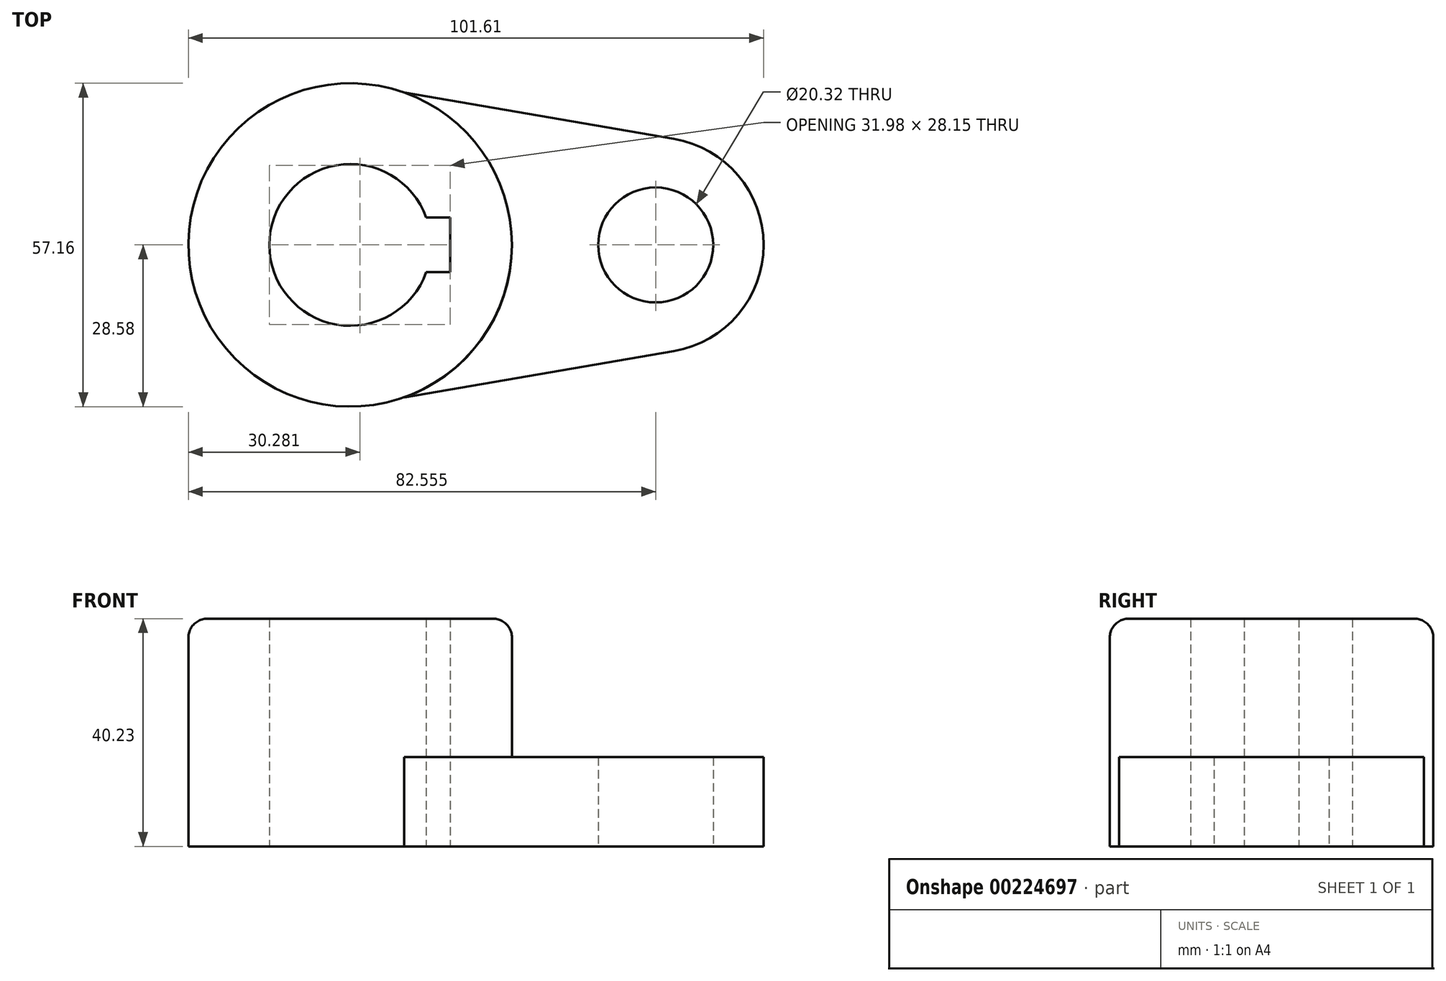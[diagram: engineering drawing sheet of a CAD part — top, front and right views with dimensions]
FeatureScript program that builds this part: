
annotation { "Feature Type Name" : "Feature", "Feature Type Description" : "" }
export const myFeature = defineFeature(function(context is Context, id is Id, definition is map)
    precondition{}
    {
        {
            var Q0;
            Q0=qCreatedBy(makeId("Top.planeOp"),FACE);
            var sketch = newSketch(context, id + "F0", { "sketchPlane" : qUnion([Q0])});
            skArc(sketch, "E0", {"start": v(13.45, 4.83) * mm, "mid": v(-14.29, 0) * mm, "end": v(13.45, -4.83) * mm});
            skCircle(sketch, "E1", {"center": v(53.98, 0) * mm, "radius": 10.16 * mm});
            skCircle(sketch, "E2", {"center": v(0, 0) * mm, "radius": 28.58 * mm});
            skLineSegment(sketch, "E3.bottom", {"start": v(17.69, 4.83) * mm, "end": v(13.45, 4.83) * mm});
            skLineSegment(sketch, "E3.top", {"start": v(17.69, -4.83) * mm, "end": v(13.45, -4.83) * mm});
            skLineSegment(sketch, "E3.left", {"start": v(17.69, 4.83) * mm, "end": v(17.69, -4.83) * mm});
            skPoint(sketch, "E3.right.end.orphan", {"position": v(-13.45, -4.83) * mm});
            skPoint(sketch, "E4.orphan", {"position": v(0, 28.58) * mm});
            skPoint(sketch, "E5.orphan", {"position": v(0, -28.58) * mm});
            skLineSegment(sketch, "E6", {"start": v(9.51, 26.95) * mm, "end": v(57.2, 18.78) * mm});
            skLineSegment(sketch, "E7", {"start": v(9.51, -26.95) * mm, "end": v(57.2, -18.78) * mm});
            skArc(sketch, "E8", {"start": v(57.2, 18.78) * mm, "mid": v(73.03, 0) * mm, "end": v(57.2, -18.78) * mm});
            skCircle(sketch, "E9", {"center": v(0, 0) * mm, "radius": 26.9 * mm});
            skSolve(sketch);
        }
        {
            var Q0;
            Q0=makeQuery(id+"F0.imprint","IMPRINT",FACE,{"disambiguationData":[TD([[makeQuery(id+"F0.imprint","IMPRINT",EDGE,{"derivedFrom":sQuery(id+"F0.wireOp",EDGE,"E0")}),-1.0]])]});
            var Q1;
            Q1=makeQuery(id+"F0.imprint","IMPRINT",FACE,{"disambiguationData":[TD([[makeQuery(id+"F0.imprint","IMPRINT",EDGE,{"derivedFrom":sQuery(id+"F0.wireOp",EDGE,"E9")}),-1.0]])]});
            extrude(context, id + "F1", {"entities" : qUnion([Q0, Q1]), "depth" : 40.23 * mm});
        }
        {
            var Q0;
            Q0=makeQuery(id+"F0.imprint","IMPRINT",FACE,{"disambiguationData":[TD([[makeQuery(id+"F0.imprint","IMPRINT",EDGE,{"derivedFrom":sQuery(id+"F0.wireOp",EDGE,"E1")}),-1.0]])]});
            extrude(context, id + "F2", {"entities" : qUnion([Q0]), "operationType" : NewBodyOperationType.ADD, "depth" : 15.77 * mm});
        }
        {
            var Q0;
            Q0=makeQuery(id+"F1.opExtrude","CAP_EDGE",EDGE,{"disambiguationData":[OSD([sQuery(id+"F0.wireOp",EDGE,"E2")])],"isStart":false});
            fillet(context, id + "F3", {"entities" : qUnion([Q0]), "radius" : 3.3 * mm, "tangentPropagation" : true, "allowEdgeOverflow" : false});
        }
    });
